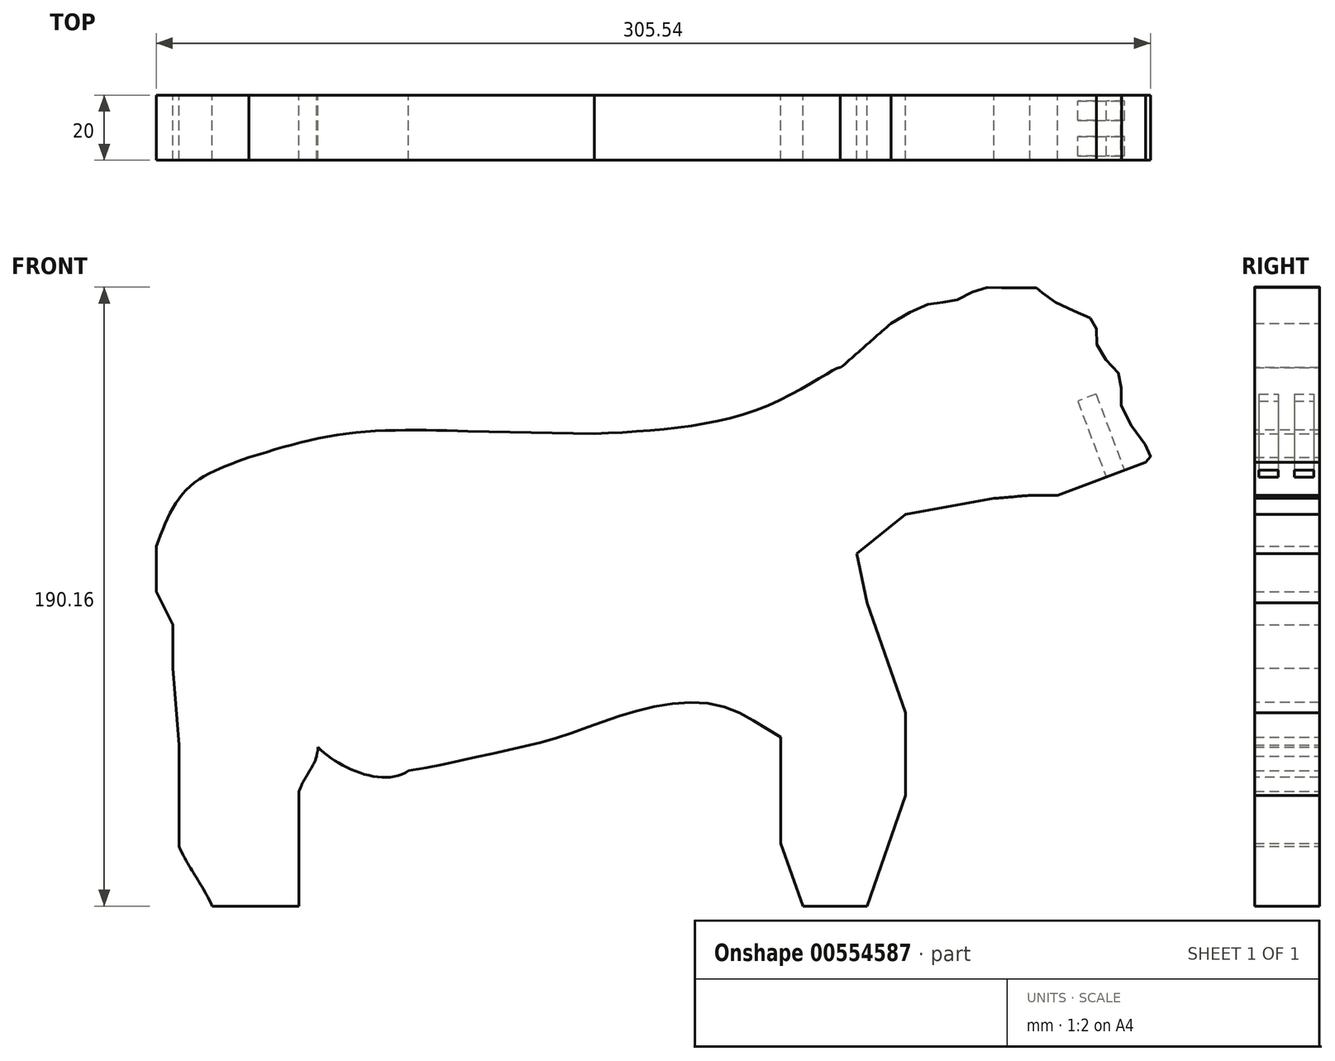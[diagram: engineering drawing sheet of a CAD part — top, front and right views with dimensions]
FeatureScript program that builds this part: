
annotation { "Feature Type Name" : "Feature", "Feature Type Description" : "" }
export const myFeature = defineFeature(function(context is Context, id is Id, definition is map)
    precondition{}
    {
        {
            var Q0;
            Q0=qCreatedBy(makeId("Front.planeOp"),FACE);
            var sketch = newSketch(context, id + "F0", { "sketchPlane" : qUnion([Q0])});
            skFitSpline(sketch, "E0", {"points": [v(-79.8, 30.45) * mm, v(-70.2, 48.15) * mm, v(-51.3, 57.75) * mm], "startDerivative": vector(15.04, 40.03) * mm, "endDerivative": vector(41.85, 14.68) * mm});
            skFitSpline(sketch, "E1", {"points": [v(-51.3, 57.75) * mm, v(-21.79, 65) * mm, v(15.97, 65.84) * mm], "startDerivative": vector(60.24, 18.57) * mm, "endDerivative": vector(74.06, -2) * mm});
            skFitSpline(sketch, "E2", {"points": [v(15.97, 65.84) * mm, v(54.83, 65) * mm], "startDerivative": vector(38.86, -0.85) * mm, "endDerivative": vector(38.86, -0.85) * mm});
            skFitSpline(sketch, "E3", {"points": [v(54.83, 65) * mm, v(106.92, 73.17) * mm, v(129.75, 85.28) * mm, v(130.47, 85.28) * mm], "startDerivative": vector(99.37, 5.16) * mm, "endDerivative": vector(7.95, -2.72) * mm});
            skFitSpline(sketch, "E4", {"points": [v(130.47, 85.28) * mm, v(146.03, 98.92) * mm], "startDerivative": vector(16.41, 14.13) * mm, "endDerivative": vector(16.41, 14.13) * mm});
            skLineSegment(sketch, "E5", {"start": v(177.65, 45.16) * mm, "end": v(150.5, 40.26) * mm});
            skLineSegment(sketch, "E6", {"start": v(150.5, 40.26) * mm, "end": v(135.44, 28.18) * mm});
            skLineSegment(sketch, "E7", {"start": v(135.44, 28.18) * mm, "end": v(138.62, 13.06) * mm});
            skLineSegment(sketch, "E8", {"start": v(138.62, 13.06) * mm, "end": v(150.5, -20.66) * mm});
            skLineSegment(sketch, "E9", {"start": v(150.5, -20.66) * mm, "end": v(150.5, -46.15) * mm});
            skLineSegment(sketch, "E10", {"start": v(150.5, -46.15) * mm, "end": v(138.62, -80.1) * mm});
            skLineSegment(sketch, "E11", {"start": v(138.62, -80.1) * mm, "end": v(118.93, -80.1) * mm});
            skLineSegment(sketch, "E12", {"start": v(118.93, -80.1) * mm, "end": v(112.13, -60.78) * mm});
            skLineSegment(sketch, "E13", {"start": v(112.13, -60.78) * mm, "end": v(112.13, -28.22) * mm});
            skFitSpline(sketch, "E14", {"points": [v(112.13, -28.22) * mm, v(93.05, -18.41) * mm, v(66.4, -20.51) * mm, v(43.94, -28.22) * mm, v(21.86, -33.6) * mm, v(-2.26, -38.52) * mm], "startDerivative": vector(-98.76, 54.87) * mm, "endDerivative": vector(-125.15, -20.4) * mm});
            skFitSpline(sketch, "E15", {"points": [v(146.03, 98.92) * mm, v(158.33, 105.09) * mm, v(165.55, 105.94) * mm, v(174.03, 109.76) * mm, v(181.67, 109.76) * mm, v(191, 109.76) * mm, v(192.27, 108.48) * mm, v(201.6, 102.97) * mm, v(208.82, 98.92) * mm, v(209.67, 91.09) * mm, v(216.46, 82.6) * mm, v(216.88, 73.27) * mm, v(225.37, 59.7) * mm, v(225.37, 57.15) * mm, v(223.67, 55.87) * mm], "startDerivative": vector(137.53, 84.85) * mm, "endDerivative": vector(-52.23, -29.94) * mm});
            skFitSpline(sketch, "E16", {"points": [v(188.73, 46.09) * mm, v(177.65, 45.16) * mm], "startDerivative": vector(-9.53, -0.53) * mm, "endDerivative": vector(-9.53, -0.53) * mm});
            skFitSpline(sketch, "E17", {"points": [v(-30.07, -31.3) * mm, v(-30.46, -34.07) * mm], "startDerivative": vector(0, -5.1) * mm, "endDerivative": vector(0, -5.1) * mm});
            skFitSpline(sketch, "E18", {"points": [v(-30.46, -34.07) * mm, v(-35.98, -44.88) * mm], "startDerivative": vector(-5.52, -14.42) * mm, "endDerivative": vector(-5.52, -14.42) * mm});
            skFitSpline(sketch, "E19", {"points": [v(-35.98, -44.88) * mm, v(-35.98, -65.24) * mm], "startDerivative": vector(0, -20.36) * mm, "endDerivative": vector(0, -20.36) * mm});
            skFitSpline(sketch, "E20", {"points": [v(-35.98, -70.56) * mm, v(-35.98, -80.1) * mm], "startDerivative": vector(0, -13.15) * mm, "endDerivative": vector(0, -13.15) * mm});
            skFitSpline(sketch, "E21", {"points": [v(-2.26, -38.52) * mm, v(-30.07, -31.3) * mm], "startDerivative": vector(-22.08, -15.9) * mm, "endDerivative": vector(-19.17, 19.73) * mm});
            skFitSpline(sketch, "E22", {"points": [v(-35.98, -80.1) * mm, v(-62.62, -80.1) * mm], "startDerivative": vector(-26.64, 0) * mm, "endDerivative": vector(-26.64, 0) * mm});
            skFitSpline(sketch, "E23", {"points": [v(-62.62, -80.1) * mm, v(-72.82, -61.78) * mm], "startDerivative": vector(-10.2, 21.93) * mm, "endDerivative": vector(-10.2, 21.93) * mm});
            skFitSpline(sketch, "E24", {"points": [v(-72.82, -61.78) * mm, v(-72.82, -30.58) * mm], "startDerivative": vector(0, 31.2) * mm, "endDerivative": vector(0, 31.2) * mm});
            skFitSpline(sketch, "E25", {"points": [v(-79.8, 16.57) * mm, v(-74.74, 6.31) * mm], "startDerivative": vector(5.06, -10.25) * mm, "endDerivative": vector(5.06, -10.25) * mm});
            skFitSpline(sketch, "E26", {"points": [v(-74.74, 6.31) * mm, v(-74.74, -6.96) * mm], "startDerivative": vector(0, -13.28) * mm, "endDerivative": vector(0, -13.28) * mm});
            skFitSpline(sketch, "E27", {"points": [v(-74.74, -6.96) * mm, v(-72.82, -30.58) * mm], "startDerivative": vector(1.92, -23.61) * mm, "endDerivative": vector(1.92, -23.61) * mm});
            skFitSpline(sketch, "E28", {"points": [v(-35.98, -70.56) * mm, v(-35.98, -65.24) * mm], "startDerivative": vector(0, 5.31) * mm, "endDerivative": vector(0, 5.31) * mm});
            skFitSpline(sketch, "E29", {"points": [v(-79.8, 30.45) * mm, v(-79.8, 16.57) * mm], "startDerivative": vector(0, -13.88) * mm, "endDerivative": vector(0, -13.88) * mm});
            skFitSpline(sketch, "E30", {"points": [v(188.73, 46.09) * mm, v(197.22, 46.09) * mm], "startDerivative": vector(8.49, 0) * mm, "endDerivative": vector(8.49, 0) * mm});
            skFitSpline(sketch, "E31", {"points": [v(224.32, 56.25) * mm, v(197.22, 46.09) * mm], "startDerivative": vector(-27.1, -10.16) * mm, "endDerivative": vector(-27.1, -10.16) * mm});
            skSolve(sketch);
        }
        {
            var Q0;
            Q0 = qSketchRegion(id + "F0", true);
            extrude(context, id + "F1", {"entities" : qUnion([Q0]), "depth" : 20 * mm, "offsetDistance" : 25 * mm});
        }
        {
            var Q0;
            Q0=makeQuery(id+"F1.opExtrude","SWEPT_FACE",FACE,{"disambiguationData":[OSD([sQuery(id+"F0.wireOp",EDGE,"E31")])]});
            var sketch = newSketch(context, id + "F2", { "sketchPlane" : qUnion([Q0])});
            skLineSegment(sketch, "E32.bottom", {"start": v(222.8, 18.71) * mm, "end": v(216.8, 18.71) * mm});
            skLineSegment(sketch, "E32.top", {"start": v(222.8, 12.71) * mm, "end": v(216.8, 12.71) * mm});
            skLineSegment(sketch, "E32.left", {"start": v(222.8, 18.71) * mm, "end": v(222.8, 12.71) * mm});
            skLineSegment(sketch, "E32.right", {"start": v(216.8, 18.71) * mm, "end": v(216.8, 12.71) * mm});
            skLineSegment(sketch, "E33.bottom", {"start": v(222.8, 7.78) * mm, "end": v(216.8, 7.78) * mm});
            skLineSegment(sketch, "E33.top", {"start": v(222.8, 1.78) * mm, "end": v(216.8, 1.78) * mm});
            skLineSegment(sketch, "E33.left", {"start": v(222.8, 7.78) * mm, "end": v(222.8, 1.78) * mm});
            skLineSegment(sketch, "E33.right", {"start": v(216.8, 7.78) * mm, "end": v(216.8, 1.78) * mm});
            skSolve(sketch);
        }
        {
            var Q0;
            Q0 = qSketchRegion(id + "F2", true);
            extrude(context, id + "F3", {"entities" : qUnion([Q0]), "operationType" : NewBodyOperationType.REMOVE, "oppositeDirection" : true, "depth" : 25 * mm, "offsetDistance" : 25 * mm});
        }
    });
